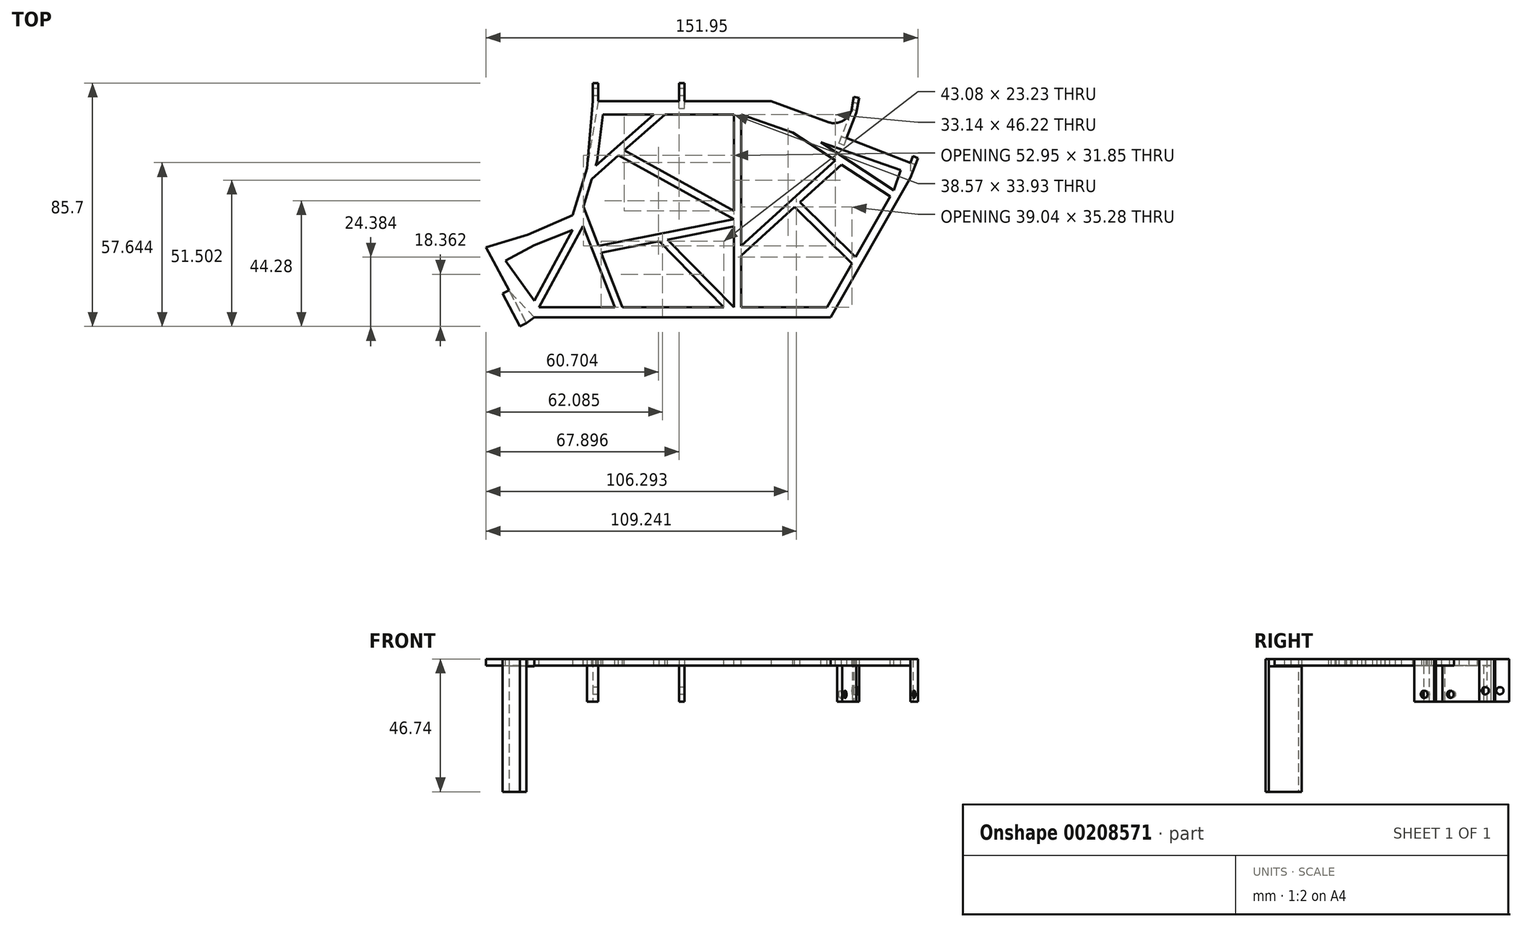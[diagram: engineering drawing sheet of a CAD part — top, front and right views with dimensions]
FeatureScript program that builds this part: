
annotation { "Feature Type Name" : "Feature", "Feature Type Description" : "" }
export const myFeature = defineFeature(function(context is Context, id is Id, definition is map)
    precondition{}
    {
        {
            var Q0;
            Q0=qCreatedBy(makeId("Top.planeOp"),FACE);
            var sketch = newSketch(context, id + "F0", { "sketchPlane" : qUnion([Q0])});
            skLineSegment(sketch, "E0", {"start": v(-31, -29.13) * mm, "end": v(-39.75, -19.88) * mm});
            skLineSegment(sketch, "E1", {"start": v(-39.75, -19.88) * mm, "end": v(-48, -4.38) * mm});
            skLineSegment(sketch, "E2", {"start": v(-48, -4.38) * mm, "end": v(-33.25, 0) * mm});
            skLineSegment(sketch, "E3", {"start": v(-33.25, 0) * mm, "end": v(-17.5, 6.88) * mm});
            skLineSegment(sketch, "E4", {"start": v(-17.5, 6.88) * mm, "end": v(-12.44, 23.38) * mm});
            skLineSegment(sketch, "E5", {"start": v(-12.44, 23.38) * mm, "end": v(-10.46, 47.02) * mm});
            skLineSegment(sketch, "E6", {"start": v(-10.46, 47.02) * mm, "end": v(19.98, 47.02) * mm});
            skLineSegment(sketch, "E7", {"start": v(19.98, 47.02) * mm, "end": v(21.89, 47.02) * mm});
            skLineSegment(sketch, "E8", {"start": v(21.89, 47.02) * mm, "end": v(52.33, 47.02) * mm});
            skLineSegment(sketch, "E9", {"start": v(50.42, 47.02) * mm, "end": v(52.33, 47.02) * mm});
            skLineSegment(sketch, "E10", {"start": v(78.88, 34.03) * mm, "end": v(101.32, 25.34) * mm});
            skLineSegment(sketch, "E11", {"start": v(101.32, 25.34) * mm, "end": v(101.32, 20.06) * mm});
            skLineSegment(sketch, "E12", {"start": v(73.3, -29.13) * mm, "end": v(-31, -29.13) * mm});
            skLineSegment(sketch, "E13", {"start": v(-10.46, 47.02) * mm, "end": v(-10.46, 53.42) * mm});
            skLineSegment(sketch, "E14", {"start": v(-10.46, 53.42) * mm, "end": v(-8.56, 53.42) * mm});
            skLineSegment(sketch, "E15", {"start": v(-8.56, 53.42) * mm, "end": v(-8.56, 47.02) * mm});
            skLineSegment(sketch, "E16", {"start": v(19.98, 47.02) * mm, "end": v(19.98, 53.42) * mm});
            skLineSegment(sketch, "E17", {"start": v(19.98, 53.42) * mm, "end": v(21.89, 53.42) * mm});
            skLineSegment(sketch, "E18", {"start": v(21.89, 53.42) * mm, "end": v(21.89, 47.02) * mm});
            skLineSegment(sketch, "E19", {"start": v(52.33, 47.02) * mm, "end": v(53.46, 53.42) * mm});
            skLineSegment(sketch, "E20", {"start": v(50.42, 53.42) * mm, "end": v(53.46, 53.42) * mm});
            skLineSegment(sketch, "E21", {"start": v(50.42, 53.42) * mm, "end": v(50.42, 47.02) * mm});
            skLineSegment(sketch, "E22", {"start": v(101.32, 25.34) * mm, "end": v(102.22, 27.67) * mm});
            skLineSegment(sketch, "E23", {"start": v(78.88, 34.03) * mm, "end": v(82.33, 42.94) * mm});
            skLineSegment(sketch, "E24", {"start": v(81.95, 41.95) * mm, "end": v(81.95, 41.95) * mm});
            skLineSegment(sketch, "E25", {"start": v(-8.56, 47.02) * mm, "end": v(-12.44, 23.38) * mm});
            skLineSegment(sketch, "E26", {"start": v(101.32, 20.06) * mm, "end": v(73.3, -29.13) * mm});
            skLineSegment(sketch, "E27", {"start": v(52.33, 47.02) * mm, "end": v(72.33, 39.67) * mm});
            skPoint(sketch, "E28.visualSharp", {"position": v(80.87, 36.53) * mm});
            skArc(sketch, "E28.filletArc", {"start": v(72.33, 39.67) * mm, "mid": v(78.15, 40.43) * mm, "end": v(80.87, 45.63) * mm});
            skLineSegment(sketch, "E29", {"start": v(77.1, 34.72) * mm, "end": v(80.44, 43.34) * mm});
            skLineSegment(sketch, "E30.trimOffspring", {"start": v(80.87, 36.53) * mm, "end": v(79.94, 36.77) * mm});
            skLineSegment(sketch, "E31", {"start": v(77.1, 34.72) * mm, "end": v(75.55, 30.7) * mm});
            skLineSegment(sketch, "E32", {"start": v(78.88, 34.03) * mm, "end": v(77.32, 30.01) * mm});
            skLineSegment(sketch, "E33.trimOffspring", {"start": v(77.32, 30.01) * mm, "end": v(75.55, 30.7) * mm});
            skLineSegment(sketch, "E34", {"start": v(80.87, 45.63) * mm, "end": v(81.37, 48.5) * mm});
            skLineSegment(sketch, "E35", {"start": v(83.25, 48.16) * mm, "end": v(82.33, 42.94) * mm});
            skLineSegment(sketch, "E36", {"start": v(81.37, 48.5) * mm, "end": v(83.25, 48.16) * mm});
            skLineSegment(sketch, "E37", {"start": v(102.22, 27.67) * mm, "end": v(103.95, 27) * mm});
            skLineSegment(sketch, "E38", {"start": v(103.95, 27) * mm, "end": v(101.32, 20.06) * mm});
            skSolve(sketch);
        }
        {
            var Q0;
            Q0=makeQuery(id+"F0.imprint","IMPRINT",FACE,{"disambiguationData":[TD([[makeQuery(id+"F0.imprint","IMPRINT",EDGE,{"derivedFrom":sQuery(id+"F0.wireOp",EDGE,"E0")}),-1.0]])]});
            extrude(context, id + "F1", {"entities" : qUnion([Q0]), "depth" : 2.3 * mm});
        }
        {
            var Q0;
            Q0=makeQuery(id+"F1.opExtrude","SWEPT_FACE",FACE,{"disambiguationData":[OSD([sQuery(id+"F0.wireOp",EDGE,"E1")])]});
            extrude(context, id + "F2", {"entities" : qUnion([Q0]), "operationType" : NewBodyOperationType.ADD, "depth" : 2.54 * mm});
        }
        {
            var Q0;
            {var subQ0=sQuery(id+"F0.wireOp",EDGE,"E1");Q0=makeQuery(id+"F2.boolean.opBoolean","MERGE",FACE,{"derivedFrom":[makeQuery(id+"F1.opExtrude","CAP_FACE",FACE,{"disambiguationData":[OSD([sQuery(id+"F0.wireOp",EDGE,"E0"),subQ0,sQuery(id+"F0.wireOp",EDGE,"E2"),sQuery(id+"F0.wireOp",EDGE,"E3"),sQuery(id+"F0.wireOp",EDGE,"E4"),sQuery(id+"F0.wireOp",EDGE,"E5"),sQuery(id+"F0.wireOp",EDGE,"E6"),sQuery(id+"F0.wireOp",EDGE,"E7"),sQuery(id+"F0.wireOp",EDGE,"E8"),sQuery(id+"F0.wireOp",EDGE,"E9"),sQuery(id+"F0.wireOp",EDGE,"Z6BVu5QH-QCkj-nSfa-ycm3-ATUJHwOnQc9L"),sQuery(id+"F0.wireOp",EDGE,"gOa2JuiZ-ftmC-C1Kl-UHV4-N59OWx0Y029x"),sQuery(id+"F0.wireOp",EDGE,"2z9sh8BZ-pXlE-iVox-05nI-Wz6UF6kldvik"),sQuery(id+"F0.wireOp",EDGE,"E10"),sQuery(id+"F0.wireOp",EDGE,"E11"),sQuery(id+"F0.wireOp",EDGE,"1caMNtZA-G7ol-i3R9-29DB-hnI8cseJxYJI"),sQuery(id+"F0.wireOp",EDGE,"F9uQi5bi-b3LG-jjoe-fc2M-G8NzwKMoDne7"),sQuery(id+"F0.wireOp",EDGE,"b73xFBgr-y8Wc-Jy8l-Mwi3-qHQenAbzGYJH"),sQuery(id+"F0.wireOp",EDGE,"E12"),sQuery(id+"F0.wireOp",EDGE,"GW7FKY3f-zCZq-edOa-X7Qy-HLTkGfWuUoQk")])],"isStart":true}),makeQuery(id+"F2.opExtrude","SWEPT_FACE",FACE,{"disambiguationData":[OSD([subQ0]),TDD([makeQuery(id+"F1.opExtrude","CAP_EDGE",EDGE,{"disambiguationData":[OSD([subQ0])],"isStart":true})])]})]});}
            var sketch = newSketch(context, id + "F3", { "sketchPlane" : qUnion([Q0])});
            skLineSegment(sketch, "E39", {"start": v(-48, 4.38) * mm, "end": v(-39.75, 19.88) * mm});
            skSolve(sketch);
        }
        {
            var Q0;
            Q0=makeQuery(id+"F3.imprint","IMPRINT",FACE,{"disambiguationData":[TD([[makeQuery(id+"F3.imprint","IMPRINT",EDGE,{"derivedFrom":sQuery(id+"F3.wireOp",EDGE,"E39")}),1.0]])]});
            extrude(context, id + "F4", {"entities" : qUnion([Q0]), "operationType" : NewBodyOperationType.ADD, "depth" : 44.45 * mm});
        }
        {
            var Q0;
            Q0=makeQuery(id+"F0.imprint","IMPRINT",FACE,{"disambiguationData":[TD([[makeQuery(id+"F0.imprint","IMPRINT",EDGE,{"derivedFrom":sQuery(id+"F0.wireOp",EDGE,"E11")}),1.0]])]});
            var Q1;
            {var subQ0=sQuery(id+"F0.wireOp",EDGE,"gOa2JuiZ-ftmC-C1Kl-UHV4-N59OWx0Y029x");Q1=makeQuery(id+"F0.imprint","IMPRINT",FACE,{"disambiguationData":[TD([[makeQuery(id+"F0.imprint","IMPRINT",EDGE,{"derivedFrom":subQ0}),1.0]])]});}
            var Q2;
            Q2=makeQuery(id+"F0.imprint","IMPRINT",FACE,{"disambiguationData":[TD([[makeQuery(id+"F0.imprint","IMPRINT",EDGE,{"derivedFrom":sQuery(id+"F0.wireOp",EDGE,"E9")}),1.0]])]});
            var Q3;
            Q3=makeQuery(id+"F0.imprint","IMPRINT",FACE,{"disambiguationData":[TD([[makeQuery(id+"F0.imprint","IMPRINT",EDGE,{"derivedFrom":sQuery(id+"F0.wireOp",EDGE,"E7")}),1.0]])]});
            var Q4;
            {var subQ0=sQuery(id+"F0.wireOp",EDGE,"E13");Q4=makeQuery(id+"F0.imprint","IMPRINT",FACE,{"disambiguationData":[TD([[makeQuery(id+"F0.imprint","IMPRINT",EDGE,{"derivedFrom":subQ0}),-1.0]])]});}
            var Q5;
            Q5=makeQuery(id+"F0.imprint","IMPRINT",FACE,{"disambiguationData":[TD([[makeQuery(id+"F0.imprint","IMPRINT",EDGE,{"derivedFrom":sQuery(id+"F0.wireOp",EDGE,"E5")}),1.0]])]});
            var Q6;
            Q6=makeQuery(id+"F0.imprint","IMPRINT",FACE,{"disambiguationData":[TD([[makeQuery(id+"F0.imprint","IMPRINT",EDGE,{"derivedFrom":sQuery(id+"F0.wireOp",EDGE,"E23")}),1.0]])]});
            var Q7;
            {var subQ0=sQuery(id+"F0.wireOp",EDGE,"E5");Q7=makeQuery(id+"F0.imprint","IMPRINT",FACE,{"disambiguationData":[TD([[makeQuery(id+"F0.imprint","IMPRINT",EDGE,{"derivedFrom":subQ0}),-1.0]])]});}
            extrude(context, id + "F5", {"entities" : qUnion([Q0, Q1, Q2, Q3, Q4, Q5, Q6, Q7]), "operationType" : NewBodyOperationType.ADD, "depth" : 2.3 * mm, "hasSecondDirection" : true, "secondDirectionOppositeDirection" : true, "secondDirectionDepth" : 12.7 * mm});
        }
        {
            var Q0;
            Q0=makeQuery(id+"F5.opExtrude","SWEPT_FACE",FACE,{"disambiguationData":[OSD([sQuery(id+"F0.wireOp",EDGE,"E13")])]});
            var sketch = newSketch(context, id + "F6", { "sketchPlane" : qUnion([Q0])});
            skLineSegment(sketch, "E40", {"start": v(-53.42, -8.9) * mm, "end": v(-47.02, -8.9) * mm});
            skPoint(sketch, "E41", {"position": v(-50.22, -8.9) * mm});
            skSolve(sketch);
        }
        {
            var Q0;
            Q0=sQuery(id+"F6.wireOp",VERTEX,"E41");
            var Q1;
            Q1=makeQuery(id+"F1.opExtrude","SWEPT_BODY",BODY,{"disambiguationData":[OSD([sQuery(id+"F0.wireOp",EDGE,"E0"),sQuery(id+"F0.wireOp",EDGE,"E1"),sQuery(id+"F0.wireOp",EDGE,"E2"),sQuery(id+"F0.wireOp",EDGE,"E3"),sQuery(id+"F0.wireOp",EDGE,"E4"),sQuery(id+"F0.wireOp",EDGE,"E5"),sQuery(id+"F0.wireOp",EDGE,"E6"),sQuery(id+"F0.wireOp",EDGE,"E7"),sQuery(id+"F0.wireOp",EDGE,"E8"),sQuery(id+"F0.wireOp",EDGE,"E9"),sQuery(id+"F0.wireOp",EDGE,"Z6BVu5QH-QCkj-nSfa-ycm3-ATUJHwOnQc9L"),sQuery(id+"F0.wireOp",EDGE,"gOa2JuiZ-ftmC-C1Kl-UHV4-N59OWx0Y029x"),sQuery(id+"F0.wireOp",EDGE,"2z9sh8BZ-pXlE-iVox-05nI-Wz6UF6kldvik"),sQuery(id+"F0.wireOp",EDGE,"E10"),sQuery(id+"F0.wireOp",EDGE,"E11"),sQuery(id+"F0.wireOp",EDGE,"1caMNtZA-G7ol-i3R9-29DB-hnI8cseJxYJI"),sQuery(id+"F0.wireOp",EDGE,"F9uQi5bi-b3LG-jjoe-fc2M-G8NzwKMoDne7"),sQuery(id+"F0.wireOp",EDGE,"b73xFBgr-y8Wc-Jy8l-Mwi3-qHQenAbzGYJH"),sQuery(id+"F0.wireOp",EDGE,"E12"),sQuery(id+"F0.wireOp",EDGE,"GW7FKY3f-zCZq-edOa-X7Qy-HLTkGfWuUoQk")])]});
            hole(context, id + "F7", {"style" : HoleStyle.SIMPLE, "endStyle" : HoleEndStyle.BLIND, "holeDiameter" : 2.54 * mm, "holeDepth" : 61.98 * mm, "locations" : qUnion([Q0]), "scope" : qUnion([Q1])});
        }
        {
            var Q0;
            Q0=makeQuery(id+"F5.opExtrude","SWEPT_FACE",FACE,{"disambiguationData":[OSD([sQuery(id+"F0.wireOp",EDGE,"E38")])]});
            var sketch = newSketch(context, id + "F8", { "sketchPlane" : qUnion([Q0])});
            skPoint(sketch, "E42", {"position": v(58.45, -10.16) * mm});
            skSolve(sketch);
        }
        {
            var Q0;
            Q0=sQuery(id+"F8.wireOp",VERTEX,"E42");
            var Q1;
            Q1=makeQuery(id+"F1.opExtrude","SWEPT_BODY",BODY,{"disambiguationData":[OSD([sQuery(id+"F0.wireOp",EDGE,"E0"),sQuery(id+"F0.wireOp",EDGE,"E1"),sQuery(id+"F0.wireOp",EDGE,"E2"),sQuery(id+"F0.wireOp",EDGE,"E3"),sQuery(id+"F0.wireOp",EDGE,"E4"),sQuery(id+"F0.wireOp",EDGE,"E5"),sQuery(id+"F0.wireOp",EDGE,"E6"),sQuery(id+"F0.wireOp",EDGE,"E7"),sQuery(id+"F0.wireOp",EDGE,"E8"),sQuery(id+"F0.wireOp",EDGE,"E9"),sQuery(id+"F0.wireOp",EDGE,"Z6BVu5QH-QCkj-nSfa-ycm3-ATUJHwOnQc9L"),sQuery(id+"F0.wireOp",EDGE,"gOa2JuiZ-ftmC-C1Kl-UHV4-N59OWx0Y029x"),sQuery(id+"F0.wireOp",EDGE,"2z9sh8BZ-pXlE-iVox-05nI-Wz6UF6kldvik"),sQuery(id+"F0.wireOp",EDGE,"E10"),sQuery(id+"F0.wireOp",EDGE,"E11"),sQuery(id+"F0.wireOp",EDGE,"1caMNtZA-G7ol-i3R9-29DB-hnI8cseJxYJI"),sQuery(id+"F0.wireOp",EDGE,"F9uQi5bi-b3LG-jjoe-fc2M-G8NzwKMoDne7"),sQuery(id+"F0.wireOp",EDGE,"b73xFBgr-y8Wc-Jy8l-Mwi3-qHQenAbzGYJH"),sQuery(id+"F0.wireOp",EDGE,"E12"),sQuery(id+"F0.wireOp",EDGE,"GW7FKY3f-zCZq-edOa-X7Qy-HLTkGfWuUoQk")])]});
            hole(context, id + "F9", {"style" : HoleStyle.SIMPLE, "endStyle" : HoleEndStyle.BLIND, "holeDiameter" : 2.54 * mm, "holeDepth" : 33.02 * mm, "locations" : qUnion([Q0]), "scope" : qUnion([Q1])});
        }
        {
            var Q0;
            Q0=makeQuery(id+"F5.opExtrude","SWEPT_FACE",FACE,{"disambiguationData":[OSD([sQuery(id+"F0.wireOp",EDGE,"E9")])]});
            var Q1;
            Q1=makeQuery(id+"F5.opExtrude","SWEPT_FACE",FACE,{"disambiguationData":[OSD([sQuery(id+"F0.wireOp",EDGE,"E7")])]});
            extrude(context, id + "F10", {"entities" : qUnion([Q0, Q1]), "operationType" : NewBodyOperationType.ADD, "depth" : 2.54 * mm});
        }
        {
            var Q0;
            {var subQ0=sQuery(id+"F0.wireOp",EDGE,"E1");Q0=makeQuery(id+"F2.boolean.opBoolean","MERGE",FACE,{"derivedFrom":[makeQuery(id+"F1.opExtrude","CAP_FACE",FACE,{"disambiguationData":[OSD([sQuery(id+"F0.wireOp",EDGE,"E0"),subQ0,sQuery(id+"F0.wireOp",EDGE,"E2"),sQuery(id+"F0.wireOp",EDGE,"E3"),sQuery(id+"F0.wireOp",EDGE,"E4"),sQuery(id+"F0.wireOp",EDGE,"E6"),sQuery(id+"F0.wireOp",EDGE,"E7"),sQuery(id+"F0.wireOp",EDGE,"E8"),sQuery(id+"F0.wireOp",EDGE,"E9"),sQuery(id+"F0.wireOp",EDGE,"E10"),sQuery(id+"F0.wireOp",EDGE,"E11"),sQuery(id+"F0.wireOp",EDGE,"E12"),sQuery(id+"F0.wireOp",EDGE,"E25"),sQuery(id+"F0.wireOp",EDGE,"E26"),sQuery(id+"F0.wireOp",EDGE,"E27"),sQuery(id+"F0.wireOp",EDGE,"E28.filletArc"),sQuery(id+"F0.wireOp",EDGE,"E29"),sQuery(id+"F0.wireOp",EDGE,"E31"),sQuery(id+"F0.wireOp",EDGE,"E32"),sQuery(id+"F0.wireOp",EDGE,"E33.trimOffspring")])],"isStart":false}),makeQuery(id+"F2.opExtrude","SWEPT_FACE",FACE,{"disambiguationData":[OSD([subQ0]),TDD([makeQuery(id+"F1.opExtrude","CAP_EDGE",EDGE,{"disambiguationData":[OSD([subQ0])],"isStart":false})])]})]});}
            var sketch = newSketch(context, id + "F11", { "sketchPlane" : qUnion([Q0])});
            skLineSegment(sketch, "E43", {"start": v(-6.84, 42.33) * mm, "end": v(41.72, 42.33) * mm});
            skLineSegment(sketch, "E44", {"start": v(41.72, 42.33) * mm, "end": v(97.89, 22.71) * mm});
            skLineSegment(sketch, "E45", {"start": v(97.89, 22.71) * mm, "end": v(95.43, 15.67) * mm});
            skLineSegment(sketch, "E46", {"start": v(95.43, 15.67) * mm, "end": v(71.96, -25.53) * mm});
            skLineSegment(sketch, "E47", {"start": v(71.96, -25.53) * mm, "end": v(-29.35, -25.53) * mm});
            skLineSegment(sketch, "E48", {"start": v(-29.35, -25.53) * mm, "end": v(-41.2, -9.08) * mm});
            skLineSegment(sketch, "E49", {"start": v(-41.2, -9.08) * mm, "end": v(-31, -3.66) * mm});
            skLineSegment(sketch, "E50", {"start": v(-31, -3.66) * mm, "end": v(-13.83, 3.07) * mm});
            skLineSegment(sketch, "E51", {"start": v(-13.83, 3.07) * mm, "end": v(-13.77, 9.94) * mm});
            skLineSegment(sketch, "E52", {"start": v(-13.83, 3.07) * mm, "end": v(-29.35, -25.53) * mm});
            skLineSegment(sketch, "E53", {"start": v(-17.5, 1.63) * mm, "end": v(-31, -23.25) * mm});
            skLineSegment(sketch, "E54", {"start": v(-13.83, 3.07) * mm, "end": v(-2.72, -25.53) * mm});
            skLineSegment(sketch, "E55", {"start": v(0, -25.53) * mm, "end": v(-13.77, 9.94) * mm});
            skLineSegment(sketch, "E56", {"start": v(-9.46, 24.22) * mm, "end": v(11.1, 42.33) * mm});
            skLineSegment(sketch, "E57", {"start": v(-10.85, 19.6) * mm, "end": v(14.93, 42.33) * mm});
            skLineSegment(sketch, "E58", {"start": v(95.43, 15.67) * mm, "end": v(69.8, 32.52) * mm});
            skLineSegment(sketch, "E59", {"start": v(94.17, 13.46) * mm, "end": v(59.95, 35.96) * mm});
            skLineSegment(sketch, "E60", {"start": v(41.72, 42.33) * mm, "end": v(41.72, -25.53) * mm});
            skLineSegment(sketch, "E61", {"start": v(39.18, 42.33) * mm, "end": v(39.18, -25.53) * mm});
            skLineSegment(sketch, "E62", {"start": v(0.61, 29.7) * mm, "end": v(39.18, 8.4) * mm});
            skLineSegment(sketch, "E63", {"start": v(-1.41, 27.92) * mm, "end": v(39.18, 5.5) * mm});
            skLineSegment(sketch, "E64", {"start": v(-8.39, -3.92) * mm, "end": v(39.18, 5.5) * mm});
            skPoint(sketch, "E65.endSnap0", {"position": v(-6.89, -7.8) * mm});
            skLineSegment(sketch, "E66", {"start": v(74.87, 26.15) * mm, "end": v(41.72, -3.89) * mm});
            skLineSegment(sketch, "E67", {"start": v(77.06, 24.71) * mm, "end": v(41.72, -7.32) * mm});
            skLineSegment(sketch, "E68", {"start": v(82.06, -7.8) * mm, "end": v(62.43, 11.45) * mm});
            skLineSegment(sketch, "E69", {"start": v(60.54, 9.74) * mm, "end": v(80.76, -10.08) * mm});
            skLineSegment(sketch, "E70", {"start": v(39.18, 2.9) * mm, "end": v(-7.46, -6.33) * mm});
            skLineSegment(sketch, "E71", {"start": v(39.18, -25.53) * mm, "end": v(15.86, -1.71) * mm});
            skLineSegment(sketch, "E72", {"start": v(35.63, -25.53) * mm, "end": v(12.89, -2.3) * mm});
            skPoint(sketch, "E73", {"position": v(-6.84, 42.33) * mm});
            skPoint(sketch, "E74.orphan", {"position": v(-13.71, 17.09) * mm});
            skLineSegment(sketch, "E75", {"start": v(-6.84, 42.33) * mm, "end": v(-8.89, 26.11) * mm});
            skLineSegment(sketch, "E76", {"start": v(-8.89, 26.11) * mm, "end": v(-13.77, 9.94) * mm});
            skPoint(sketch, "E77", {"position": v(41.72, -3.89) * mm});
            skSolve(sketch);
        }
        {
            var Q0;
            {var subQ3=sQuery(id+"F11.wireOp",EDGE,"E63");Q0=makeQuery(id+"F11.imprint","IMPRINT",FACE,{"disambiguationData":[TD([[makeQuery(id+"F11.imprint","IMPRINT",EDGE,{"derivedFrom":subQ3}),-1.0]])]});}
            var Q1;
            {var subQ0=sQuery(id+"F11.wireOp",EDGE,"XW1hXaPo-RyUY-air6-Wdwl-tk0w2k2kVIwS");Q1=makeQuery(id+"F11.imprint","IMPRINT",FACE,{"disambiguationData":[TD([[makeQuery(id+"F11.imprint","IMPRINT",EDGE,{"derivedFrom":subQ0}),-1.0]])]});}
            var Q2;
            {var subQ5=sQuery(id+"F11.wireOp",EDGE,"E62");Q2=makeQuery(id+"F11.imprint","IMPRINT",FACE,{"disambiguationData":[TD([[makeQuery(id+"F11.imprint","IMPRINT",EDGE,{"derivedFrom":subQ5}),1.0]])]});}
            var Q3;
            {var subQ5=sQuery(id+"F11.wireOp",EDGE,"E66");Q3=makeQuery(id+"F11.imprint","IMPRINT",FACE,{"disambiguationData":[TD([[makeQuery(id+"F11.imprint","IMPRINT",EDGE,{"derivedFrom":subQ5}),-1.0]])]});}
            var Q4;
            {var subQ3=sQuery(id+"F11.wireOp",EDGE,"E68");Q4=makeQuery(id+"F11.imprint","IMPRINT",FACE,{"disambiguationData":[TD([[makeQuery(id+"F11.imprint","IMPRINT",EDGE,{"derivedFrom":subQ3}),-1.0]])]});}
            var Q5;
            {var subQ0=sQuery(id+"F11.wireOp",EDGE,"E45");Q5=makeQuery(id+"F11.imprint","IMPRINT",FACE,{"disambiguationData":[TD([[makeQuery(id+"F11.imprint","IMPRINT",EDGE,{"derivedFrom":subQ0}),-1.0]])]});}
            var Q6;
            {var subQ7=sQuery(id+"F11.wireOp",EDGE,"E69");Q6=makeQuery(id+"F11.imprint","IMPRINT",FACE,{"disambiguationData":[TD([[makeQuery(id+"F11.imprint","IMPRINT",EDGE,{"derivedFrom":subQ7}),-1.0]])]});}
            var Q7;
            {var subQ0=sQuery(id+"F11.wireOp",EDGE,"E71");Q7=makeQuery(id+"F11.imprint","IMPRINT",FACE,{"disambiguationData":[TD([[makeQuery(id+"F11.imprint","IMPRINT",EDGE,{"derivedFrom":subQ0}),-1.0]])]});}
            var Q8;
            {var subQ3=sQuery(id+"F11.wireOp",EDGE,"E72");Q8=makeQuery(id+"F11.imprint","IMPRINT",FACE,{"disambiguationData":[TD([[makeQuery(id+"F11.imprint","IMPRINT",EDGE,{"derivedFrom":subQ3}),1.0]])]});}
            var Q9;
            {var subQ0=sQuery(id+"F11.wireOp",EDGE,"E52");Q9=makeQuery(id+"F11.imprint","IMPRINT",FACE,{"disambiguationData":[TD([[makeQuery(id+"F11.imprint","IMPRINT",EDGE,{"derivedFrom":subQ0}),1.0]])]});}
            var Q10;
            {var subQ0=sQuery(id+"F11.wireOp",EDGE,"E49");Q10=makeQuery(id+"F11.imprint","IMPRINT",FACE,{"disambiguationData":[TD([[makeQuery(id+"F11.imprint","IMPRINT",EDGE,{"derivedFrom":subQ0}),-1.0]])]});}
            var Q11;
            {var subQ2=sQuery(id+"F11.wireOp",EDGE,"E56");Q11=makeQuery(id+"F11.imprint","IMPRINT",FACE,{"disambiguationData":[TD([[makeQuery(id+"F11.imprint","IMPRINT",EDGE,{"derivedFrom":subQ2}),1.0]])]});}
            extrude(context, id + "F12", {"entities" : qUnion([Q0, Q1, Q2, Q3, Q4, Q5, Q6, Q7, Q8, Q9, Q10, Q11]), "operationType" : NewBodyOperationType.REMOVE, "endBound" : BoundingType.THROUGH_ALL, "oppositeDirection" : true, "depth" : 25.4 * mm});
        }
        {
            var Q0;
            Q0=makeQuery(id+"F5.opExtrude","SWEPT_FACE",FACE,{"disambiguationData":[OSD([sQuery(id+"F0.wireOp",EDGE,"E35")])]});
            var sketch = newSketch(context, id + "F13", { "sketchPlane" : qUnion([Q0])});
            skLineSegment(sketch, "E78", {"start": v(61.89, -8.9) * mm, "end": v(56.58, -8.9) * mm});
            skPoint(sketch, "E79", {"position": v(58.71, -8.9) * mm});
            skSolve(sketch);
        }
        {
            var Q0;
            Q0=sQuery(id+"F13.wireOp",VERTEX,"E79");
            var Q1;
            Q1=makeQuery(id+"F1.opExtrude","SWEPT_BODY",BODY,{"disambiguationData":[OSD([sQuery(id+"F0.wireOp",EDGE,"E0"),sQuery(id+"F0.wireOp",EDGE,"E1"),sQuery(id+"F0.wireOp",EDGE,"E2"),sQuery(id+"F0.wireOp",EDGE,"E3"),sQuery(id+"F0.wireOp",EDGE,"E4"),sQuery(id+"F0.wireOp",EDGE,"E6"),sQuery(id+"F0.wireOp",EDGE,"E7"),sQuery(id+"F0.wireOp",EDGE,"E8"),sQuery(id+"F0.wireOp",EDGE,"E9"),sQuery(id+"F0.wireOp",EDGE,"E10"),sQuery(id+"F0.wireOp",EDGE,"E11"),sQuery(id+"F0.wireOp",EDGE,"E12"),sQuery(id+"F0.wireOp",EDGE,"E25"),sQuery(id+"F0.wireOp",EDGE,"E26"),sQuery(id+"F0.wireOp",EDGE,"E27"),sQuery(id+"F0.wireOp",EDGE,"E28.filletArc"),sQuery(id+"F0.wireOp",EDGE,"E29"),sQuery(id+"F0.wireOp",EDGE,"E31"),sQuery(id+"F0.wireOp",EDGE,"E32"),sQuery(id+"F0.wireOp",EDGE,"E33.trimOffspring")])]});
            hole(context, id + "F14", {"style" : HoleStyle.SIMPLE, "endStyle" : HoleEndStyle.BLIND, "holeDiameter" : 2.54 * mm, "holeDepth" : 29.84 * mm, "locations" : qUnion([Q0]), "scope" : qUnion([Q1])});
        }
        {
            var Q0;
            {var subQ0=sQuery(id+"F0.wireOp",EDGE,"E1");var subQ1=sQuery(id+"F0.wireOp",EDGE,"E0");Q0=makeQuery(id+"F4.boolean.opBoolean","MERGE",FACE,{"derivedFrom":[makeQuery(id+"F2.opExtrude","SWEPT_FACE",FACE,{"disambiguationData":[OSD([subQ1,subQ0])]}),makeQuery(id+"F4.opExtrude","SWEPT_FACE",FACE,{"disambiguationData":[OSD([subQ1,subQ0])]})]});}
            extrude(context, id + "F15", {"entities" : qUnion([Q0]), "operationType" : NewBodyOperationType.ADD, "depth" : 12.7 * mm});
        }
        {
            var Q0;
            {var subQ0=sQuery(id+"F0.wireOp",EDGE,"E2");var subQ1=sQuery(id+"F0.wireOp",EDGE,"E1");Q0=makeQuery(id+"F4.boolean.opBoolean","MERGE",FACE,{"derivedFrom":[makeQuery(id+"F2.opExtrude","SWEPT_FACE",FACE,{"disambiguationData":[OSD([subQ1,subQ0])]}),makeQuery(id+"F4.opExtrude","SWEPT_FACE",FACE,{"disambiguationData":[OSD([subQ1,subQ0])]})]});}
            extrude(context, id + "F16", {"entities" : qUnion([Q0]), "operationType" : NewBodyOperationType.REMOVE, "oppositeDirection" : true, "depth" : 17.14 * mm});
        }
        {
            var Q0;
            {var subQ0=sQuery(id+"F0.wireOp",EDGE,"E1");var subQ1=sQuery(id+"F0.wireOp",EDGE,"E0");var subQ2=sQuery(id+"F0.wireOp",EDGE,"E33.trimOffspring");var subQ3=sQuery(id+"F0.wireOp",EDGE,"E32");var subQ4=sQuery(id+"F0.wireOp",EDGE,"E31");var subQ5=sQuery(id+"F0.wireOp",EDGE,"E29");var subQ6=sQuery(id+"F0.wireOp",EDGE,"E28.filletArc");var subQ7=sQuery(id+"F0.wireOp",EDGE,"E11");var subQ8=sQuery(id+"F0.wireOp",EDGE,"E9");var subQ9=sQuery(id+"F0.wireOp",EDGE,"E7");var subQ10=sQuery(id+"F0.wireOp",EDGE,"E25");Q0=makeQuery(id+"F15.boolean.opBoolean","MERGE",FACE,{"derivedFrom":[makeQuery(id+"F5.boolean.opBoolean","MERGE",FACE,{"derivedFrom":[makeQuery(id+"F2.boolean.opBoolean","MERGE",FACE,{"derivedFrom":[makeQuery(id+"F1.opExtrude","CAP_FACE",FACE,{"disambiguationData":[OSD([subQ1,subQ0,sQuery(id+"F0.wireOp",EDGE,"E2"),sQuery(id+"F0.wireOp",EDGE,"E3"),sQuery(id+"F0.wireOp",EDGE,"E4"),sQuery(id+"F0.wireOp",EDGE,"E6"),subQ9,sQuery(id+"F0.wireOp",EDGE,"E8"),subQ8,sQuery(id+"F0.wireOp",EDGE,"E10"),subQ7,sQuery(id+"F0.wireOp",EDGE,"E12"),subQ10,sQuery(id+"F0.wireOp",EDGE,"E26"),sQuery(id+"F0.wireOp",EDGE,"E27"),subQ6,subQ5,subQ4,subQ3,subQ2])],"isStart":false}),makeQuery(id+"F2.opExtrude","SWEPT_FACE",FACE,{"disambiguationData":[OSD([subQ0]),TDD([makeQuery(id+"F1.opExtrude","CAP_EDGE",EDGE,{"disambiguationData":[OSD([subQ0])],"isStart":false})])]})]}),makeQuery(id+"F5.opExtrude","CAP_FACE",FACE,{"disambiguationData":[OSD([sQuery(id+"F0.wireOp",EDGE,"E5"),sQuery(id+"F0.wireOp",EDGE,"E13"),sQuery(id+"F0.wireOp",EDGE,"E14"),sQuery(id+"F0.wireOp",EDGE,"E15"),subQ10])],"isStart":false}),makeQuery(id+"F5.opExtrude","CAP_FACE",FACE,{"disambiguationData":[OSD([subQ9,sQuery(id+"F0.wireOp",EDGE,"E16"),sQuery(id+"F0.wireOp",EDGE,"E17"),sQuery(id+"F0.wireOp",EDGE,"E18")])],"isStart":false}),makeQuery(id+"F5.opExtrude","CAP_FACE",FACE,{"disambiguationData":[OSD([subQ8,sQuery(id+"F0.wireOp",EDGE,"E19"),sQuery(id+"F0.wireOp",EDGE,"E20"),sQuery(id+"F0.wireOp",EDGE,"E21")])],"isStart":false}),makeQuery(id+"F5.opExtrude","CAP_FACE",FACE,{"disambiguationData":[OSD([subQ7,sQuery(id+"F0.wireOp",EDGE,"E22"),sQuery(id+"F0.wireOp",EDGE,"nVQXLWjT-UhSB-8pLO-0ukJ-BgT86o3EPgiI"),sQuery(id+"F0.wireOp",EDGE,"pcfI4Aoq-tAka-CfeP-hjCt-Hye7Df4Cerzf")])],"isStart":false}),makeQuery(id+"F5.opExtrude","CAP_FACE",FACE,{"disambiguationData":[OSD([sQuery(id+"F0.wireOp",EDGE,"E23"),subQ6,subQ5,subQ4,subQ3,subQ2,sQuery(id+"F0.wireOp",EDGE,"E34"),sQuery(id+"F0.wireOp",EDGE,"E35"),sQuery(id+"F0.wireOp",EDGE,"E36")])],"isStart":false})]}),makeQuery(id+"F15.opExtrude","SWEPT_FACE",FACE,{"disambiguationData":[OSD([subQ1,subQ0]),TDD([makeQuery(id+"F2.opExtrude","SWEPT_EDGE",EDGE,{"disambiguationData":[OSD([subQ1,subQ0]),TDD([makeQuery(id+"F1.opExtrude","CAP_VERTEX",VERTEX,{"disambiguationData":[OSD([subQ1,subQ0])],"isStart":false})])]})])]})]});}
            var sketch = newSketch(context, id + "F17", { "sketchPlane" : qUnion([Q0])});
            skLineSegment(sketch, "E80", {"start": v(-31, -29.13) * mm, "end": v(-33.78, -31.09) * mm});
            skLineSegment(sketch, "E81", {"start": v(-33.78, -31.09) * mm, "end": v(-39.75, -19.88) * mm});
            skLineSegment(sketch, "E82", {"start": v(-39.75, -19.88) * mm, "end": v(-31, -29.13) * mm});
            skSolve(sketch);
        }
        {
            var Q0;
            Q0=makeQuery(id+"F17.imprint","IMPRINT",FACE,{"disambiguationData":[TD([[makeQuery(id+"F17.imprint","IMPRINT",EDGE,{"derivedFrom":sQuery(id+"F17.wireOp",EDGE,"E80")}),-1.0]])]});
            extrude(context, id + "F18", {"entities" : qUnion([Q0]), "operationType" : NewBodyOperationType.ADD, "oppositeDirection" : true, "depth" : 2.54 * mm});
        }
    });
